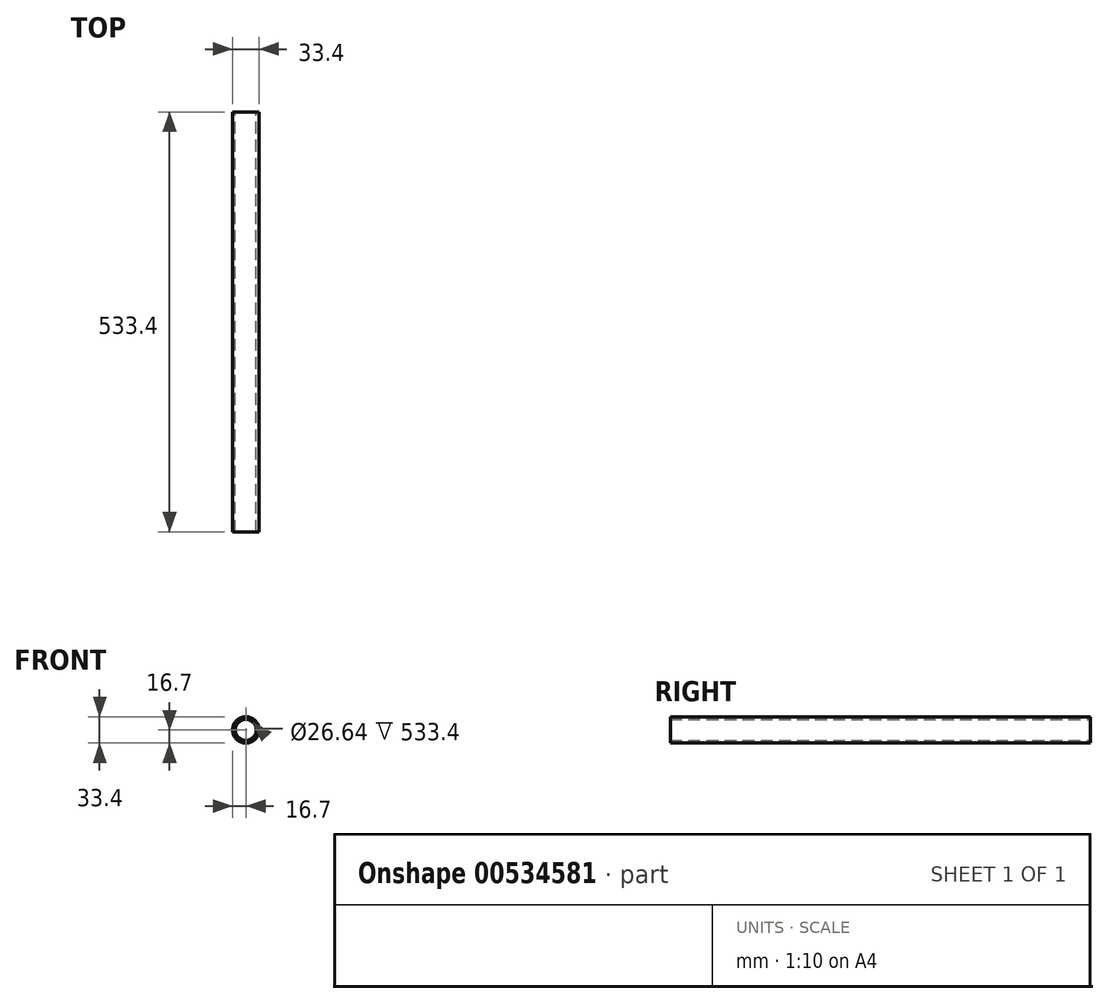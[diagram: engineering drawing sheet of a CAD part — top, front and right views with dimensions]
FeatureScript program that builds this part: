
annotation { "Feature Type Name" : "Feature", "Feature Type Description" : "" }
export const myFeature = defineFeature(function(context is Context, id is Id, definition is map)
    precondition{}
    {
        {
            var Q0;
            Q0=qCreatedBy(makeId("Front.planeOp"),FACE);
            var sketch = newSketch(context, id + "F0", { "sketchPlane" : qUnion([Q0])});
            skCircle(sketch, "E0", {"center": v(0, 0) * mm, "radius": 16.7 * mm});
            skCircle(sketch, "E1", {"center": v(0, 0) * mm, "radius": 13.32 * mm});
            skSolve(sketch);
        }
        {
            var Q0;
            Q0=makeQuery(id+"F0.imprint","IMPRINT",FACE,{"disambiguationData":[TD([[makeQuery(id+"F0.imprint","IMPRINT",EDGE,{"derivedFrom":sQuery(id+"F0.wireOp",EDGE,"E0")}),1.0]])]});
            extrude(context, id + "F1", {"entities" : qUnion([Q0]), "depth" : 533.4 * mm, "offsetDistance" : 25.4 * mm});
        }
    });
